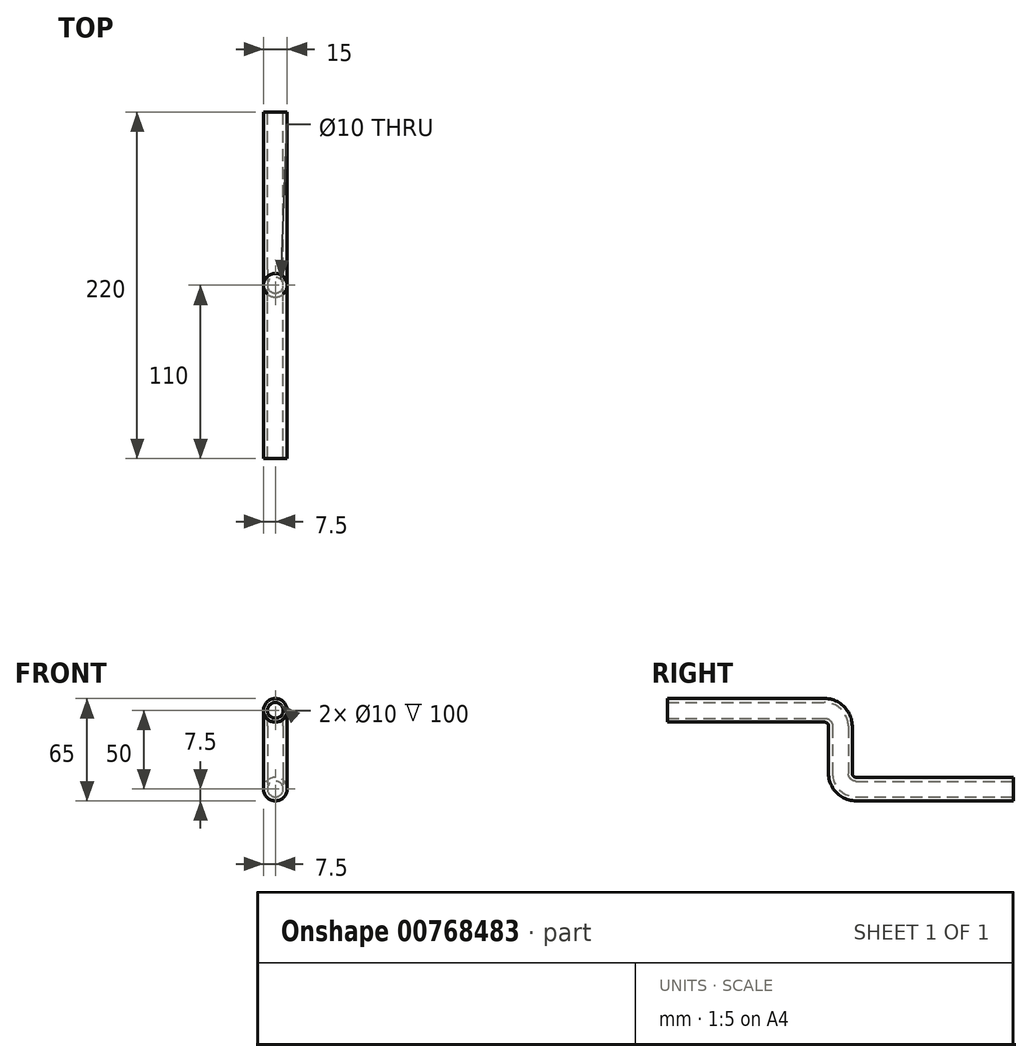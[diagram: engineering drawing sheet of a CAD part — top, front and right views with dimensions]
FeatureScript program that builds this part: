
annotation { "Feature Type Name" : "Feature", "Feature Type Description" : "" }
export const myFeature = defineFeature(function(context is Context, id is Id, definition is map)
    precondition{}
    {
        {
            var Q0;
            Q0=qCreatedBy(makeId("Front.planeOp"),FACE);
            var sketch = newSketch(context, id + "F0", { "sketchPlane" : qUnion([Q0])});
            skCircle(sketch, "E0", {"center": v(0, 0) * mm, "radius": 7.5 * mm});
            skCircle(sketch, "E1", {"center": v(0, 0) * mm, "radius": 5 * mm});
            skSolve(sketch);
        }
        {
            var Q0;
            Q0=qCreatedBy(makeId("Right.planeOp"),FACE);
            var sketch = newSketch(context, id + "F1", { "sketchPlane" : qUnion([Q0])});
            skLineSegment(sketch, "E2", {"start": v(0, 0) * mm, "end": v(100, 0) * mm});
            skLineSegment(sketch, "E3", {"start": v(110, -10) * mm, "end": v(110, -40) * mm});
            skLineSegment(sketch, "E4", {"start": v(120, -50) * mm, "end": v(220, -50) * mm});
            skPoint(sketch, "E5.visualSharp", {"position": v(110, 0) * mm});
            skArc(sketch, "E5.filletArc", {"start": v(110, -10) * mm, "mid": v(107.07, -2.93) * mm, "end": v(100, 0) * mm});
            skPoint(sketch, "E6.visualSharp", {"position": v(110, -50) * mm});
            skArc(sketch, "E6.filletArc", {"start": v(110, -40) * mm, "mid": v(112.93, -47.07) * mm, "end": v(120, -50) * mm});
            skSolve(sketch);
        }
        {
            var Q0;
            Q0=makeQuery(id+"F0.imprint","IMPRINT",FACE,{"disambiguationData":[TD([[makeQuery(id+"F0.imprint","IMPRINT",EDGE,{"derivedFrom":sQuery(id+"F0.wireOp",EDGE,"E0")}),1.0]])]});
            var Q1;
            Q1=sQuery(id+"F1.wireOp",EDGE,"E2");
            var Q2;
            Q2=sQuery(id+"F1.wireOp",EDGE,"E5.filletArc");
            var Q3;
            Q3=sQuery(id+"F1.wireOp",EDGE,"E3");
            var Q4;
            Q4=sQuery(id+"F1.wireOp",EDGE,"E6.filletArc");
            var Q5;
            Q5=sQuery(id+"F1.wireOp",EDGE,"E4");
            sweep(context, id + "F2", {"profiles" : qUnion([Q0]), "path" : qUnion([Q1, Q2, Q3, Q4, Q5])});
        }
    });
